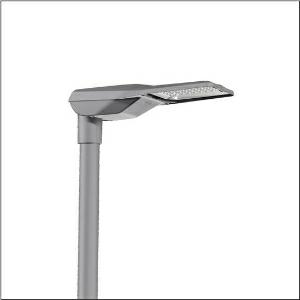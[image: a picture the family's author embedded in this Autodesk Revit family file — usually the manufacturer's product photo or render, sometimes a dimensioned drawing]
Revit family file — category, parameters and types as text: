
# Revit family: streetlight_sl_21_iq_mini___p0_5a_5xe2v31g08jb_8467
name_source: partatom
category: Lighting Fixtures
units: mm (PartAtom-declared; Revit-internal decimal feet)

## family parameters
Cut with Voids When Loaded = No
Host = Face
Light Source = No
Part Type = Normal
Room Calculation Point = No
Round Connector Dimension = Use Diameter
Shared = No

## types (1)
- --- (1 x LED, 10640 lm, 71.6 W, 3000K)
    Apparent Load = 72 VA
    CIE Flux Codes = 37 73 96 100 100
    Color Rendering = 70
    Color Temperature = 3000K
    Default Elevation = 1800 mm
    Description = Streetlight SL 21 iQ mini, mast luminaire, primary light control with lens, of PMMA, primary optical cover: cover, of toughened safety glass, transparent, light distribution: P0.5a, light emission: direct distribution, primary light characteristic: asymmetric, installation type: post-top, side-entry, LED, High Power LED, rated luminous flux: 10.640lm, luminous efficacy: 149lm/W, light colour: 730, colour temperature: 3000K, control gear: iQ Street-Remote, control: pre-setting: linear dimming characteristic, Street-Remote, Auto-Match, Temp-Guard, Lumen-Switch, Night-Set, Smart-Wire, Light-Fading, Desk-Remote (wireless, voltage-free reading and setting of iQ features in the workshop via application-optimized NFC function/RFID function), optimised constant luminous flux control (CLO 2.0), mains connection: 220..240V, AC, 50/60Hz, start of lifetime: 72W, end of service life: 75W, reduction: 33W, luminaire housing, of diecast aluminium, powder-coated, SITECO metallic grey (DB 702S), corrosivity category C5 high according to DIN EN ISO 12944, please order mast flange separately, inclination adjustable: 0°, 5°, 10°, 15°, sealing non-destructively replaceable, multi-level sealing system, length: 628mm, width: 235mm, height: 110mm, mast flange for spigot size: 42mm (side-entry): 5XC10008XM4, 60/48mm (side-entry/post-top): 5XC10108XM2, 76/60mm (side-entry/post-top): 5XC10108XM1, mounting height: 4..8m, protection rating (complete): IP66, insulation class (complete): insulation class II (safety insulation), certification: CE, ENEC, ENEC+, VDE, impact resistance: IK10, permissible operating ambient temperature for outdoor applications: -40..+50°C, standard-compliant lighting for roads and squares, packaging unit: 1 piece

Light Distribution: P0.5a
    Height = 110 mm
    Lamp = 1 x LED
    Lamp Light Flux = 10640 lm
    Lamp Power = 71.6 W
    Lamp count = 1
    Length = 625 mm
    Luminous efficacy = 149 lm/W
    Manufacturer = Siteco
    ModVariant = No
    Model = 5XE2V31G08JB
    Number of Poles = 1
    OnlyDefault = Yes
    Power Factor = 1
    Product Name = Streetlight SL 21 iQ mini | P0.5a
    Product group = mast luminaire | pylon top
    ProductGroupID = 6100
    Protection Class = Protection class II
    Protection Degree = IP 66
    RLX_Detail_Level = 1
    RLX_Emergency_Light_Flux = 0 lm
    RLX_Emergency_Type = 0
    RLX_Emergency_Type_DB = No
    RlxData = <blob elided: 92913 chars, md5=10101e5c>
    Socket = socket
    Standby Power = 0 W
    System Light Flux = 10640 lm
    System Power = 72 W
    Type Comments = factory setting: luminous flux: 100 % | dim-lin: 254 | 746 mA
    Type Image = l_1003519.jpg
    URL = http://relux.com
    VarID = @adj_076939
    Voltage = 0 V
    Weight = 0.00 kg
    Width = 234 mm

## geometry (parser evidence)
native form markers: Blend x4, Sweep x11
no freeform markers — native parametric forms only
